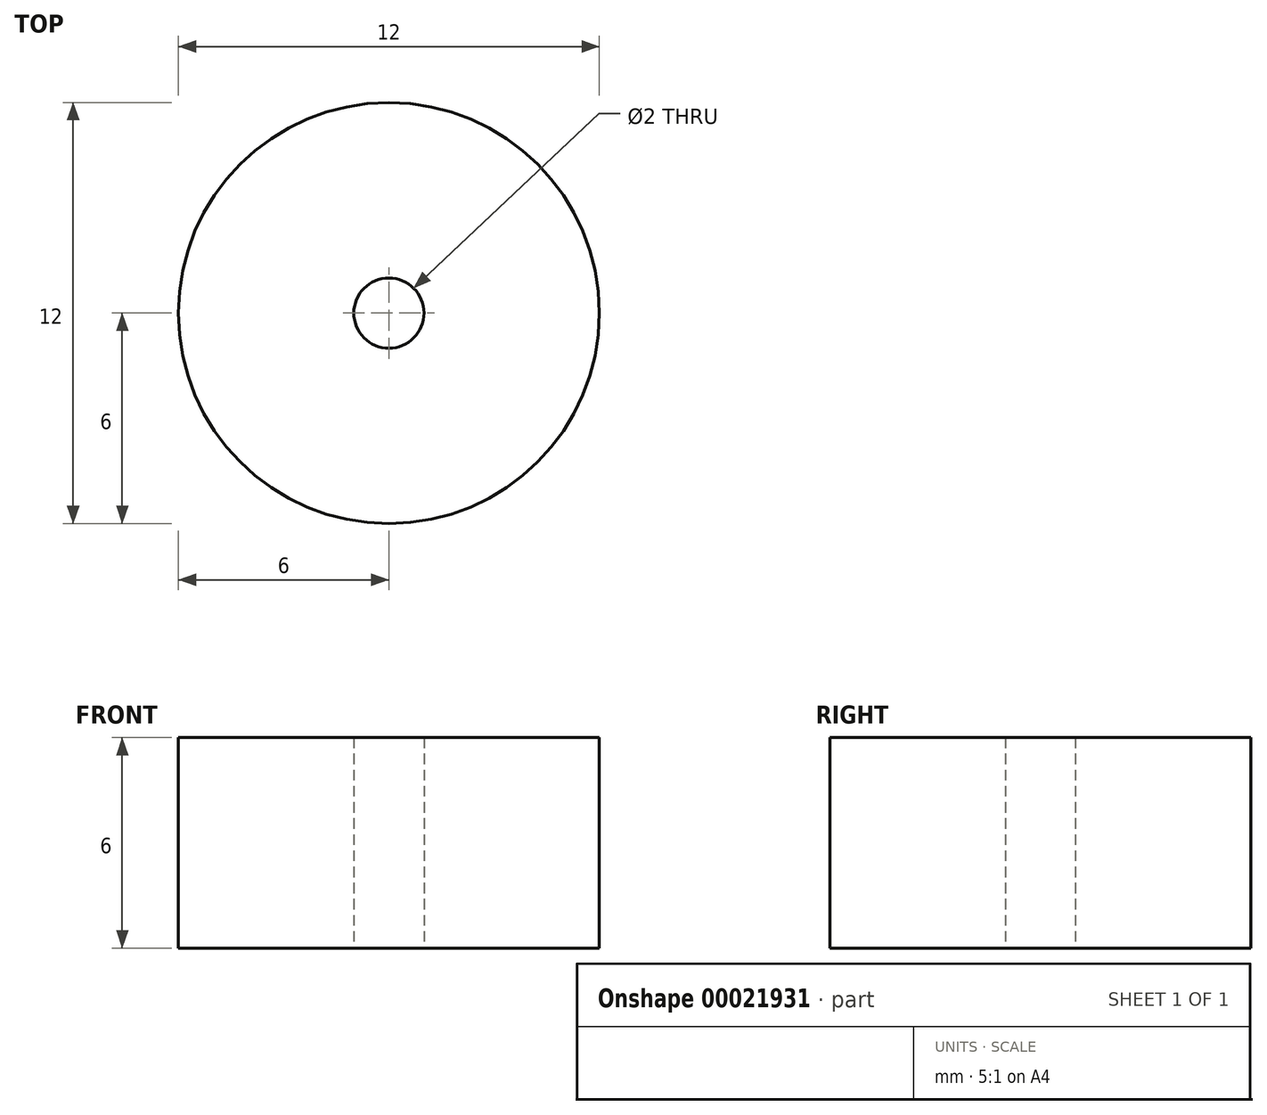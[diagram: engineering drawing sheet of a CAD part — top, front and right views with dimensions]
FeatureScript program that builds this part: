
annotation { "Feature Type Name" : "Feature", "Feature Type Description" : "" }
export const myFeature = defineFeature(function(context is Context, id is Id, definition is map)
    precondition{}
    {
        {
            var Q0;
            Q0=qCreatedBy(makeId("Top.planeOp"),FACE);
            var sketch = newSketch(context, id + "F0", { "sketchPlane" : qUnion([Q0])});
            skCircle(sketch, "E0", {"center": v(0, 0) * mm, "radius": 6 * mm});
            skCircle(sketch, "E1", {"center": v(0, 0) * mm, "radius": 1 * mm});
            skSolve(sketch);
        }
        {
            var Q0;
            Q0=makeQuery(id+"F0.imprint","IMPRINT",FACE,{"disambiguationData":[TD([[makeQuery(id+"F0.imprint","IMPRINT",EDGE,{"derivedFrom":sQuery(id+"F0.wireOp",EDGE,"E0")}),1.0]])]});
            extrude(context, id + "F1", {"entities" : qUnion([Q0]), "endBound" : BoundingType.SYMMETRIC, "depth" : 6 * mm});
        }
    });
